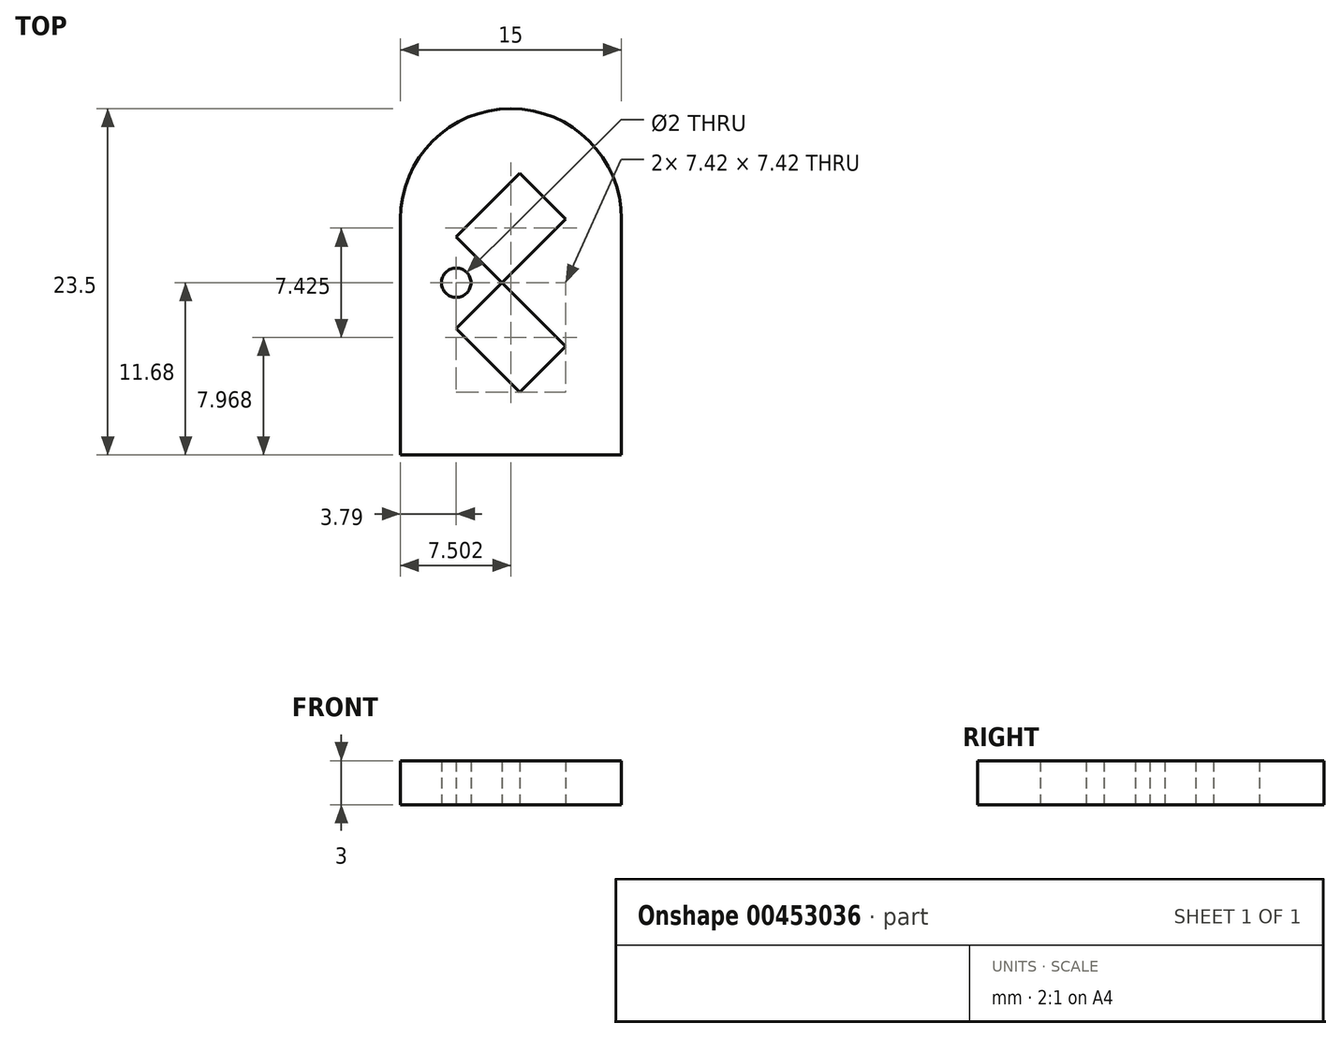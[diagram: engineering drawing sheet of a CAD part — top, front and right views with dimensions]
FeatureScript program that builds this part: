
annotation { "Feature Type Name" : "Feature", "Feature Type Description" : "" }
export const myFeature = defineFeature(function(context is Context, id is Id, definition is map)
    precondition{}
    {
        {
            var Q0;
            Q0=qCreatedBy(makeId("Top.planeOp"),FACE);
            var sketch = newSketch(context, id + "F0", { "sketchPlane" : qUnion([Q0])});
            skLineSegment(sketch, "E0.bottom", {"start": v(-7, 7) * mm, "end": v(7, 7) * mm, "construction": true});
            skLineSegment(sketch, "E0.top", {"start": v(-7, -7) * mm, "end": v(7, -7) * mm, "construction": true});
            skLineSegment(sketch, "E0.left", {"start": v(-7, 7) * mm, "end": v(-7, -7) * mm, "construction": true});
            skLineSegment(sketch, "E0.right", {"start": v(7, 7) * mm, "end": v(7, -7) * mm, "construction": true});
            skPoint(sketch, "E0.middle", {"position": v(0, 0) * mm});
            skLineSegment(sketch, "E1", {"start": v(-7, 7) * mm, "end": v(7, -7) * mm, "construction": true});
            skLineSegment(sketch, "E2", {"start": v(7, 7) * mm, "end": v(-7, -7) * mm, "construction": true});
            skCircle(sketch, "E3", {"center": v(0, 0) * mm, "radius": 1 * mm});
            skCircle(sketch, "E4.0", {"center": v(0, 0) * mm, "radius": 2.2 * mm});
            skLineSegment(sketch, "E5", {"start": v(1.56, -1.56) * mm, "end": v(3.1, 0) * mm});
            skLineSegment(sketch, "E6", {"start": v(3.1, 0) * mm, "end": v(7.42, -4.32) * mm});
            skLineSegment(sketch, "E7.MirrorCS", {"start": v(0, -3.1) * mm, "end": v(4.32, -7.42) * mm});
            skLineSegment(sketch, "E8.MirrorCS", {"start": v(1.56, -1.56) * mm, "end": v(0, -3.1) * mm});
            skLineSegment(sketch, "E9", {"start": v(4.32, -7.42) * mm, "end": v(7.42, -4.32) * mm});
            skCircle(sketch, "E10", {"center": v(0, 0) * mm, "radius": 7 * mm, "construction": true});
            skLineSegment(sketch, "E11.MirrorCS", {"start": v(3.1, 0) * mm, "end": v(7.42, 4.32) * mm});
            skLineSegment(sketch, "E12.MirrorCS", {"start": v(1.56, 1.56) * mm, "end": v(3.1, 0) * mm});
            skLineSegment(sketch, "E13.MirrorCS", {"start": v(1.56, 1.56) * mm, "end": v(0, 3.1) * mm});
            skLineSegment(sketch, "E14.MirrorCS", {"start": v(0, 3.1) * mm, "end": v(4.32, 7.42) * mm});
            skLineSegment(sketch, "E15.MirrorCS", {"start": v(4.32, 7.42) * mm, "end": v(7.42, 4.32) * mm});
            skLineSegment(sketch, "E16", {"start": v(7.42, 4.32) * mm, "end": v(0, 4.32) * mm, "construction": true});
            skArc(sketch, "E17", {"start": v(11.21, 4.32) * mm, "mid": v(3.44, 11.81) * mm, "end": v(-3.77, 3.77) * mm});
            skLineSegment(sketch, "E18", {"start": v(11.21, 4.32) * mm, "end": v(11.21, -11.68) * mm});
            skLineSegment(sketch, "E19", {"start": v(11.21, -11.68) * mm, "end": v(-3.79, -11.68) * mm});
            skLineSegment(sketch, "E20", {"start": v(-3.79, 4.32) * mm, "end": v(-3.79, -11.68) * mm});
            skSolve(sketch);
        }
        {
            var Q0;
            {var subQ3=sQuery(id+"F0.wireOp",EDGE,"E5");Q0=makeQuery(id+"F0.imprint","IMPRINT",FACE,{"disambiguationData":[TD([[makeQuery(id+"F0.imprint","IMPRINT",EDGE,{"derivedFrom":subQ3}),1.0]])]});}
            var Q1;
            {var subQ0=sQuery(id+"F0.wireOp",EDGE,"E4.0");var subQ1=makeQuery(id+"F0.imprint","INTERSECT",VERTEX,{"derivedFrom":[subQ0,sQuery(id+"F0.wireOp",EDGE,"E5"),sQuery(id+"F0.wireOp",EDGE,"E8.MirrorCS")]});Q1=makeQuery(id+"F0.imprint","IMPRINT",FACE,{"disambiguationData":[TD([[makeQuery(id+"F0.imprint","IMPRINT",EDGE,{"disambiguationData":[TD([[subQ1,1.0]])],"derivedFrom":subQ0}),1.0]])]});}
            extrude(context, id + "F1", {"entities" : qUnion([Q0, Q1]), "depth" : 3 * mm});
        }
    });
